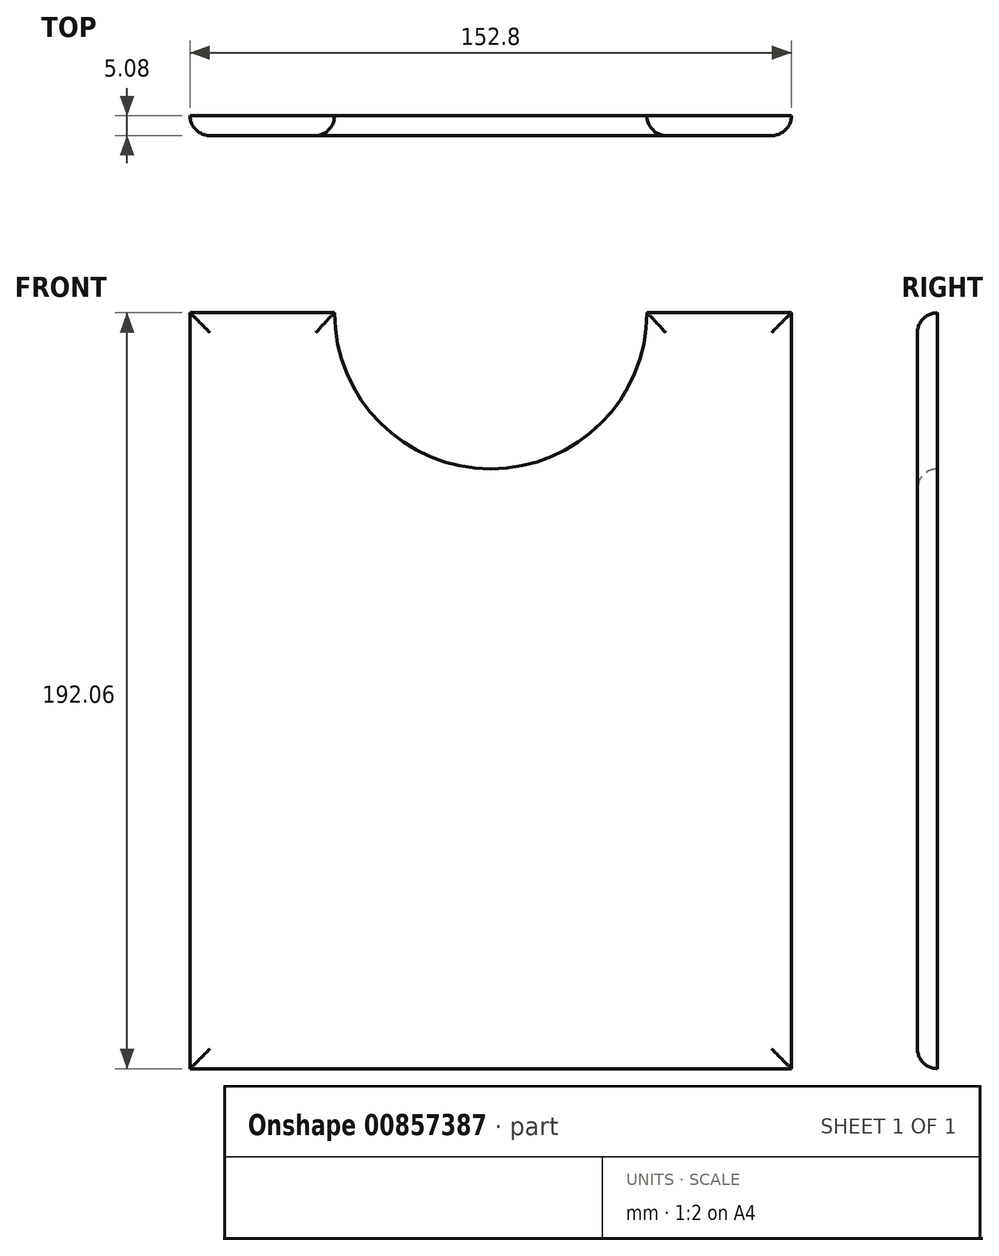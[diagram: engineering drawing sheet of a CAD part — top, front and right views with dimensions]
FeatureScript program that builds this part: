
annotation { "Feature Type Name" : "Feature", "Feature Type Description" : "" }
export const myFeature = defineFeature(function(context is Context, id is Id, definition is map)
    precondition{}
    {
        {
            var Q0;
            Q0=qCreatedBy(makeId("Front.planeOp"),FACE);
            var sketch = newSketch(context, id + "F0", { "sketchPlane" : qUnion([Q0])});
            skLineSegment(sketch, "E0.bottom", {"start": v(-76.4, 76.4) * mm, "end": v(76.4, 76.4) * mm});
            skLineSegment(sketch, "E0.top", {"start": v(-76.4, -115.66) * mm, "end": v(76.4, -115.66) * mm});
            skLineSegment(sketch, "E0.left", {"start": v(-76.4, 76.4) * mm, "end": v(-76.4, -115.66) * mm});
            skLineSegment(sketch, "E0.right", {"start": v(76.4, 76.4) * mm, "end": v(76.4, -115.66) * mm});
            skCircle(sketch, "E1", {"center": v(0, 76.4) * mm, "radius": 39.68 * mm});
            skSolve(sketch);
        }
        {
            var Q0;
            Q0=makeQuery(id+"F0.imprint","IMPRINT",FACE,{"disambiguationData":[TD([[makeQuery(id+"F0.imprint","IMPRINT",EDGE,{"derivedFrom":sQuery(id+"F0.wireOp",EDGE,"E0.bottom")}),-1.0]])]});
            extrude(context, id + "F1", {"entities" : qUnion([Q0]), "depth" : 5.08 * mm, "offsetDistance" : 25.4 * mm});
        }
        {
            var Q0;
            {var subQ0=sQuery(id+"F0.wireOp",EDGE,"E0.bottom");Q0=makeQuery(id+"F1.opExtrude","CAP_EDGE",EDGE,{"disambiguationData":[OSD([subQ0]),TDD([makeQuery(id+"F0.imprint","IMPRINT",EDGE,{"disambiguationData":[TD([[makeQuery(id+"F0.imprint","INTERSECT",VERTEX,{"derivedFrom":[subQ0,sQuery(id+"F0.wireOp",EDGE,"E0.left")]}),-1.0]])],"derivedFrom":subQ0})])],"isStart":false});}
            var Q1;
            Q1=makeQuery(id+"F1.opExtrude","CAP_EDGE",EDGE,{"disambiguationData":[OSD([sQuery(id+"F0.wireOp",EDGE,"E0.left")])],"isStart":false});
            var Q2;
            Q2=makeQuery(id+"F1.opExtrude","CAP_EDGE",EDGE,{"disambiguationData":[OSD([sQuery(id+"F0.wireOp",EDGE,"E1")])],"isStart":false});
            var Q3;
            {var subQ0=sQuery(id+"F0.wireOp",EDGE,"E0.bottom");Q3=makeQuery(id+"F1.opExtrude","CAP_EDGE",EDGE,{"disambiguationData":[OSD([subQ0]),TDD([makeQuery(id+"F0.imprint","IMPRINT",EDGE,{"disambiguationData":[TD([[makeQuery(id+"F0.imprint","INTERSECT",VERTEX,{"derivedFrom":[subQ0,sQuery(id+"F0.wireOp",EDGE,"E0.right")]}),1.0]])],"derivedFrom":subQ0})])],"isStart":false});}
            var Q4;
            Q4=makeQuery(id+"F1.opExtrude","CAP_EDGE",EDGE,{"disambiguationData":[OSD([sQuery(id+"F0.wireOp",EDGE,"E0.right")])],"isStart":false});
            var Q5;
            Q5=makeQuery(id+"F1.opExtrude","CAP_EDGE",EDGE,{"disambiguationData":[OSD([sQuery(id+"F0.wireOp",EDGE,"E0.top")])],"isStart":false});
            fillet(context, id + "F2", {"entities" : qUnion([Q0, Q1, Q2, Q3, Q4, Q5]), "radius" : 5.08 * mm, "tangentPropagation" : true, "allowEdgeOverflow" : false});
        }
    });
